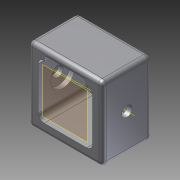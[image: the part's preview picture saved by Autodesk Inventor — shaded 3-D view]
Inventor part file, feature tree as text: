
AUTODESK INVENTOR PART (.ipt)
format: ipt  version: 2012 (Build 160160000, 160)  size: 216,064 bytes
history: native  units: mm
features: reference x9, extrude x5, sketch x5, fillet x4, plane x1, other x1, projected_geometry x1
ambient origin geometry x8: Origin, YZ Plane, XZ Plane, XY Plane, X Axis, Y Axis, Z Axis, Center Point
bodies: Solid1 (feature_tree)
feature tree (26):
  plane  "Work Plane1"
  extrude  "Extrusion1"  Depth=0.3mm
  extrude  "Extrusion2"  Depth=5.0mm
  fillet  "Fillet1"  Radius=5.0mm
  extrude  "Extrusion3"  Depth=25.0mm TaperAngle=0.0deg
  extrude  "Extrusion4"  Depth=0.3mm
  extrude  "Extrusion5"  Depth=25.0mm TaperAngle=0.0deg
  fillet  "Fillet2"  Radius=1.0mm
  fillet  "Fillet3"  Radius=12.3mm
  fillet  "Fillet4"  Radius=2.5mm
  other  "Work Axis1"
  sketch  "Sketch2"  dims[d3=0.3mm d4=0.3mm]
  reference  "Reference12"
  reference  "Reference13"
  reference  "Reference14"
  reference  "Reference15"
  sketch  "Sketch3"  dims[d5=0.3mm d6=5.0mm d7=5.0mm]
  reference  "Reference16"
  reference  "Reference17"
  reference  "Reference18"
  reference  "Reference19"
  reference  "Reference20"
  sketch  "Sketch4"  dims[d8=5.0mm d9=25.0mm d10=0.0mm]
  projected_geometry  "Projected Loop1"
  sketch  "Sketch5"  dims[d11=0.3mm d12=0.3mm]
  sketch  "Sketch6"  dims[d13=0.3mm d14=25.0mm d15=0.0mm d16=1.0mm d17=12.3mm d18=2.5mm d19=0.0mm d20=5.3mm d21=3.0mm d22=0.0mm d23=2.5mm d24=0.0mm d25=2.0mm d26=3.0mm d27=2.0mm]
